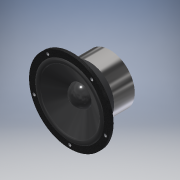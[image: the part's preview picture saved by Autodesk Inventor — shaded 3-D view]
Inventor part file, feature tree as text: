
AUTODESK INVENTOR PART (.ipt)
format: ipt  version: 2019 (Build 230136000, 136)  size: 220,160 bytes
history: native  units: mm
features: sketch x9, extrude x8, fillet x3, other x2, projected_geometry x2, hole x1, loft x1, chamfer x1
ambient origin geometry x8: Origin, YZ Plane, XZ Plane, XY Plane, X Axis, Y Axis, Z Axis, Center Point
bodies: Solid1 (feature_tree)
feature tree (27):
  extrude  "Extrusion1"  Depth=5.5mm TaperAngle=0.0deg
  hole  "Hole1"  [1 undecoded]
  extrude  "Extrusion2"  Depth=125.0mm
  extrude  "Extrusion3"  Depth=5.0mm
  loft  "Loft1"
  extrude  "Extrusion4"  Depth=90.0mm
  extrude  "Extrusion5"  Depth=2.5mm
  fillet  "Fillet1"  Radius=2.5mm
  extrude  "Extrusion6"  Depth=3.0mm
  fillet  "Fillet2"  Radius=9.0mm
  extrude  "Extrusion7"  Depth=6.0mm
  chamfer  "Chamfer1"  Distance=40.0mm
  extrude  "Extrusion8"  Depth=25.0mm TaperAngle=0.0deg
  fillet  "Fillet3"  Radius=33.5mm
  sketch  "Sketch1"  dims[d0=148.0mm d1=5.5mm d2=0.0mm]
  sketch  "Sketch2"  dims[d3=136.0mm d4=50.0mm d6=360.0deg]
  sketch  "Sketch3"  dims[d8=5.3mm d9=9.525mm d10=4.0mm d11=2.0mm d12=90.0deg d13=19.05mm d14=20.594885mm d15=125.0mm]
  sketch  "Sketch4"  dims[d16=5.0mm d17=0.0mm d18=90.0mm]
  other  "Edges1"
  other  "Edges2"
  sketch  "Sketch5"  dims[d19=25.0mm d20=0.0mm d21=0.0mm d22=90.0deg]
  sketch  "Sketch6"  dims[d23=0.0mm d24=90.0deg d25=90.0mm]
  projected_geometry  "Projected Loop1"
  sketch  "Sketch7"  dims[d26=37.5mm d27=0.0mm d28=55.0mm d31=2.5mm d32=0.0mm]
  sketch  "Sketch8"  dims[d33=3.0mm d34=125.0mm d35=9.0mm]
  sketch  "Sketch9"  dims[d36=2.5mm d37=0.0mm d38=6.0mm d39=40.0mm d40=25.0mm d41=0.0mm d42=33.5mm d43=2.0mm d44=30.0deg d45=20.0mm d46=0.0mm d47=20.0mm d48=0.0mm]
  projected_geometry  "Projected Loop2"
note: 1 required parameter value undecoded (feature->parameter linkage not recoverable at this tier; creation-order binding heuristic only, values carry confidence <= 0.55)
